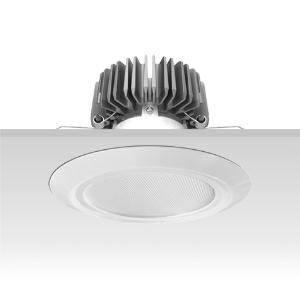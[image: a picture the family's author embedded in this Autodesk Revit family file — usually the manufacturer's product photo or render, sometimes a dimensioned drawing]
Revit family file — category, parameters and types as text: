
# Revit family: 3f_filippi_-_3f_reno_bianco_ampio_3f_filippi_-_30621_a01037_-_3f_reno_200_wh_2000-840_wide___vs_wh_7950
name_source: partatom
category: Lighting Fixtures
units: mm (PartAtom-declared; Revit-internal decimal feet)

## family parameters
Cut with Voids When Loaded = No
Host = Face
Light Source = No
Part Type = Normal
Room Calculation Point = No
Round Connector Dimension = Use Diameter
Shared = No

## types (1)
- 3F Filippi - 3F Reno Bianco Ampio (1 x LED, 1723 lm, 20 W, 4000 K)
    Apparent Load = 20 VA
    Approval mark = CE
    CIE Flux Codes = 75 94 99 100 100
    Color Rendering = 80
    Color Temperature = 4000 K
    Control Gear = Electronic ballast
    Default Elevation = 1800 mm
    Description = ILLUMINOTECHNICAL
Luminous efficiency 100% (DLOR 100%, ULOR 0%).
Initial luminous flux of the luminaire 1723 lm.
Direct symmetric wide distribution.
Installation Interdistance Transv.D = 1.16 x hu - Long.D = 1.14 x hu.
Average luminance <3000 cd/m² for radial angles >65°.
Tabular UGR (CIE 117 - 4H-8H; S=0.25H; 70/50/20): RUG 20.4 - 20.3.
Beam angle: 74° - 74°.
Luminous efficacy 86 lm/W.
Lifetime (L90/B10): 30000 h. (tq+25°C)
Lifetime (L85/B10): 50000 h. (tq+25°C)
Lifetime (L70/B10): 80000 h. (tq+25°C)
Sudden decreased luminous flux after 50000 hours: 0% (C0).
Photobiological safety in compliance with IEC/TR 62778: RG0 risk exempt, (IEC 62471).
In compliance with IEC/EN 62722-2-1 - IEC/EN 62717 standards.

SOURCE
Compact LED module 2000/840.
Energy efficiency class (UE 2019/2020 - UE 2019/2015): D.
CIE 13.3 Colour rendering index: CRI >80 (R9 <50%).
IES TM-30 Fidelity Index: Rf = 84 Rg = 95.
CCT nominal colour temperature 4000 K.
Colour initial tolerance (MacAdam): SDCM 3.
Zhaga Book 3 compliant.

MECHANICAL
Passive heat dissipator in die-casting aluminium, oversized, for optimum thermal management of the LED module.
Parabolic element with graduated/concentric rings in white polycarbonate.
Transparent external lens with glossy and satin differentiated surfaces, with a cooling and anti-insect system in methacrylate (PMMA).
Fastening spring clips in stainless steel.
Dimensions: diameter 226 mm, height 146 mm. Weight 1.155 kg.
IP44 protection degree for exposed part, IP20 for recessed part.
Mechanical strength to impacts IK06 (1 joule).
Glow-wire test resistance 650°C.

ELECTRICAL
Wiring on a separate unit.
Halogen Free electronic wiring 230V-50/60Hz, power factor 0.95, THD <25%, constant output current, SELV, class II, 1 driver.
Power of the luminaire 20 W.
ENEC - CE.
SAFE FLICKER: PstLM=<1 and SVM=<0.4 (IEC TR 61547-1 and IEC TR 63158), to ensure a more comfortable and safe light.
Luminaire compliant with EN 60598-2-22 for power supply from a centralised emergency system CPSS (Central Power Supply System), not incorporated in the luminaire - high risk areas excluded. The default power and flux are 100% in AC and 100% in DC.
Ambient temperature from 0°C to +25°C.
Temperature class T6 max 85°C.
Relative humidity UR: <85%.

INSTALLATION
Pull-up recessed fitting.
False ceiling carving: 200 mm.
All accessories dedicated to this product are available on the Catalog and on our website www.3F-Filippi.com.

ACCESSORIES
A01037 - Anti-glare microprismatic VS moulded glass, tempered, not flammable, locked and in line with the trim, in white polycarbonate.

APPLICATIONS
Environments: architectural, commercial, exhibition areas, transit areas, corridors, shops, display windows, service areas.
In false ceilings with narrow voids.

WARNING
Luminaire designed for disposal/recycling at end-of-life.
Replaceable (LED only) light source by a professional. Replaceable control gear by a professional.
    Height = 0 mm  [stored 0 ft]
    Lamp = 1 x LED
    Lamp Light Flux = 1723 lm
    Lamp Power = 20 W
    Lamp count = 1
    Length = 226 mm
    Lifetime = 50000 h
    Luminous efficacy = 86 lm/W
    Manufacturer = 3F Filippi
    ModVariant = No
    Model = 3F Filippi - 30621+A01037 - 3F Reno 200 WH 2000-840 WIDE + VS WH
    Mounting Place = Ceiling
    Mounting Type = Recessed
    Number of Poles = 1
    OnlyDefault = Yes
    Power Factor = 1
    Product Name = 3F Filippi - 3F Reno Bianco Ampio
    Product group = recessed luminaire
    ProductGroupID = 4
    Protection Class = Protection class II
    Protection Degree = IP 20
    RLX_Detail_Level = 1
    RLX_Emergency_Light_Flux = 0 lm
    RLX_Emergency_Type = 0
    RLX_Emergency_Type_DB = No
    RlxData = <blob elided: 94513 chars, md5=d33aff02>
    Socket = socket
    Standby Power = 0 W
    System Light Flux = 1723 lm
    System Power = 20 W
    Type Comments = Product without accessories
    Type Image = 3ffilippi_3f_reno_200_wh_vs_smp.jpg
    URL = http://relux.com
    VarID = ---
    Voltage = 0 V
    Weight = 0.00 kg
    Width = 0 mm  [stored 0 ft]

note: [stored X ft] marks values corroborated as IEEE doubles in the binary element streams (Revit-internal decimal feet)

## geometry (parser evidence)
native form markers: Blend x4, Sweep x11
no freeform markers — native parametric forms only
